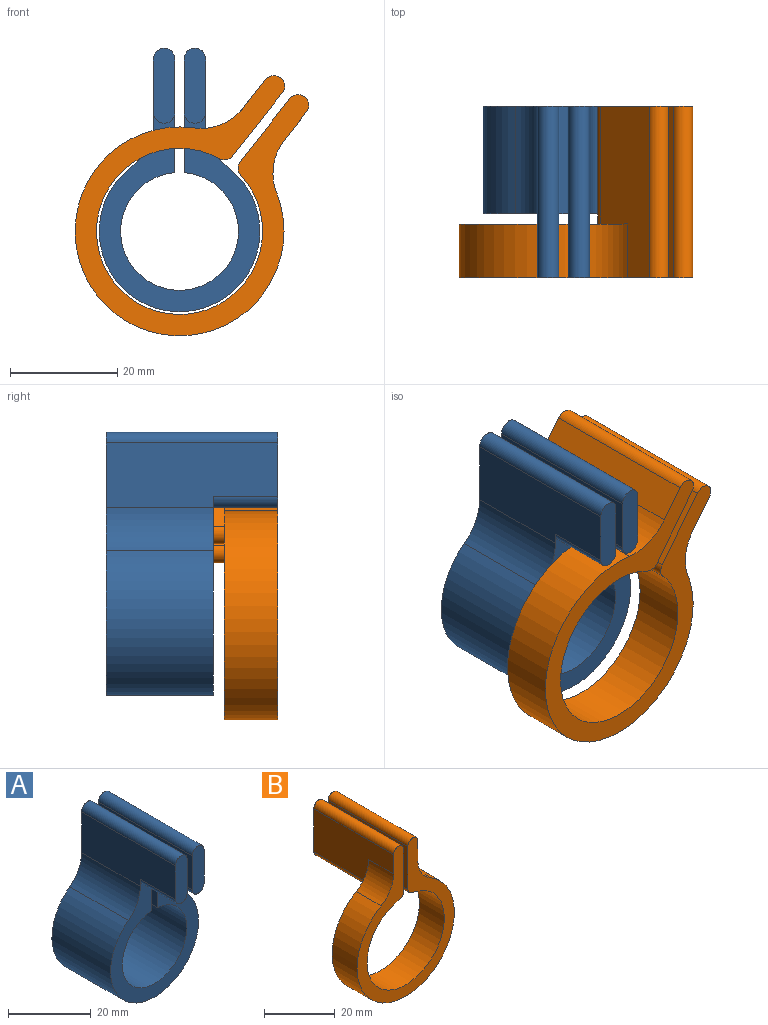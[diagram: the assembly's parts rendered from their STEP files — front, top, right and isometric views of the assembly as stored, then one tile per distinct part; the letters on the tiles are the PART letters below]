
ASSEMBLY  parts=2 mates=1
PART A: 16 faces, bbox 30x32x49.2 mm
  f0: plane 37.18x30mm, normal (0,-1,0), area 377.1mm2, adj f1,f2,f3,f4,f5,f6,f10,f11
  f1: plane 32x21.22mm, normal (1,0,0), area 544.4mm2, adj f0,f6,f7,f8,f13,f14
  f2: plane 32x12.09mm, normal (-1,0,0), area 361.9mm2, adj f0,f7,f8,f10,f13,f14
  f3: cylinder r=15mm len=30mm, axis (0,-1,0), area 1502.5mm2, adj f0,f7,f10,f11
  f4: plane 32x12.09mm, normal (1,0,0), area 361.9mm2, adj f0,f7,f9,f11,f12,f15
  f5: plane 32x21.22mm, normal (-1,0,0), area 544.4mm2, adj f0,f6,f7,f9,f12,f15
  f6: cylinder r=11mm len=22mm, axis (0,-1,0), area 1347.1mm2, adj f0,f1,f5,f7
  f7: plane 49.18x30mm, normal (0,1,0), area 482.2mm2, adj f1,f2,f3,f4,f5,f6,f10,f11
  f8: plane 14x4mm, normal (0,-1,0), area 52.6mm2, adj f1,f2,f13,f14
  f9: plane 14x4mm, normal (0,-1,0), area 52.6mm2, adj f4,f5,f12,f15
  f10: cylinder r=10mm len=20mm, axis (0,-1,0), area 186.7mm2, adj f0,f2,f3,f7
  f11: cylinder r=10mm len=20mm, axis (0,-1,0), area 186.7mm2, adj f0,f3,f4,f7
  f12: cylinder r=2mm len=12mm, axis (0,1,0), area 75.4mm2, adj f0,f4,f5,f9
  f13: cylinder r=2mm len=12mm, axis (0,1,0), area 75.4mm2, adj f0,f1,f2,f8
  f14: cylinder r=2mm len=32mm, axis (0,-1,0), area 201.1mm2, adj f1,f2,f7,f8
  f15: cylinder r=2mm len=32mm, axis (0,-1,0), area 201.1mm2, adj f4,f5,f7,f9
PART B: 16 faces, bbox 39x32x53.7 mm
  f0: plane 44.97x39mm, normal (0,1,0), area 416.5mm2, adj f1,f3,f4,f5,f10,f11,f14,f15
  f1: cylinder r=15.5mm len=31mm, axis (0,1,0), area 922.7mm2, adj f0,f7,f10,f11
  f2: plane 32x14.92mm, normal (1,0,0), area 477.5mm2, adj f7,f9,f10,f13
  f3: plane 32x14.92mm, normal (-1,0,0), area 395.4mm2, adj f0,f7,f9,f10,f13,f15
  f4: cylinder r=19.5mm len=39mm, axis (0,1,0), area 1019mm2, adj f0,f7,f14,f15
  f5: plane 32x14.92mm, normal (1,0,0), area 395.4mm2, adj f0,f7,f8,f11,f12,f14
  f6: plane 32x14.92mm, normal (-1,0,0), area 477.5mm2, adj f7,f8,f11,f12
  f7: plane 53.68x39mm, normal (0,-1,0), area 561.1mm2, adj f1,f2,f3,f4,f5,f6,f10,f11
  f8: plane 18.92x4mm, normal (0,1,0), area 72.3mm2, adj f5,f6,f11,f12
  f9: plane 18.92x4mm, normal (0,1,0), area 72.3mm2, adj f2,f3,f10,f13
  f10: cylinder r=2mm len=32mm, axis (0,1,0), area 166.3mm2, adj f0,f1,f2,f3,f7,f9
  f11: cylinder r=2mm len=32mm, axis (0,1,0), area 166.3mm2, adj f0,f1,f5,f6,f7,f8
  f12: cylinder r=2mm len=32mm, axis (0,1,0), area 201.1mm2, adj f5,f6,f7,f8
  f13: cylinder r=2mm len=32mm, axis (0,-1,0), area 201.1mm2, adj f2,f3,f7,f9
  f14: cylinder r=10mm len=10mm, axis (0,1,0), area 104.2mm2, adj f0,f4,f5,f7
  f15: cylinder r=10mm len=10mm, axis (0,1,0), area 104.2mm2, adj f0,f3,f4,f7
PLACE A at identity fixed
PLACE B rot(axis=(0,1,0),38.1deg) t=(0,-2,0)mm
MATE revolute A.f6 <-> B.f1  axis (0,-1,0) through (0,0,0)mm
